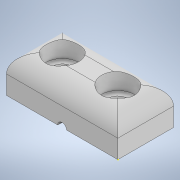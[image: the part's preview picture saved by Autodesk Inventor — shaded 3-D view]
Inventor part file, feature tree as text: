
AUTODESK INVENTOR PART (.ipt)
format: ipt  version: 2020 (Build 240168000, 168)  size: 145,920 bytes
history: native  units: in
note: dims shown in document units (in); Inventor stores cm internally (conversion verified against a paired STEP export)
features: sketch x4, hole x2, extrude x1, fillet x1
ambient origin geometry x8: Origin, YZ Plane, XZ Plane, XY Plane, X Axis, Y Axis, Z Axis, Center Point
bodies: Solid1 (feature_tree)
feature tree (8):
  extrude  "Extrusion1"  Depth=0.375in
  hole  "Hole1"  [1 undecoded]
  hole  "Hole2"  [1 undecoded]
  sketch  "Sketch4"  dims[d12=0.188in d13=0.188in d14=0.188in d15=0.129in d16=0.75in d17=0.219in d18=0.112in d19=0.5635in d20=0.25in d21=0.8108in d22=0.125in]
  fillet  "Fillet1"  Radius=0.188in
  sketch  "Sketch1"  dims[d0=0.75in d1=0.375in]
  sketch  "Sketch2"  dims[d2=0.25in d3=0.0in]
  sketch  "Sketch3"  dims[d4=0.0591in d5=0.75in d6=0.375in d7=0.25in d8=0.5635in d9=0.25in d10=0.8108in d11=0.188in]
note: 2 required parameter values undecoded (feature->parameter linkage not recoverable at this tier; creation-order binding heuristic only, values carry confidence <= 0.55)
